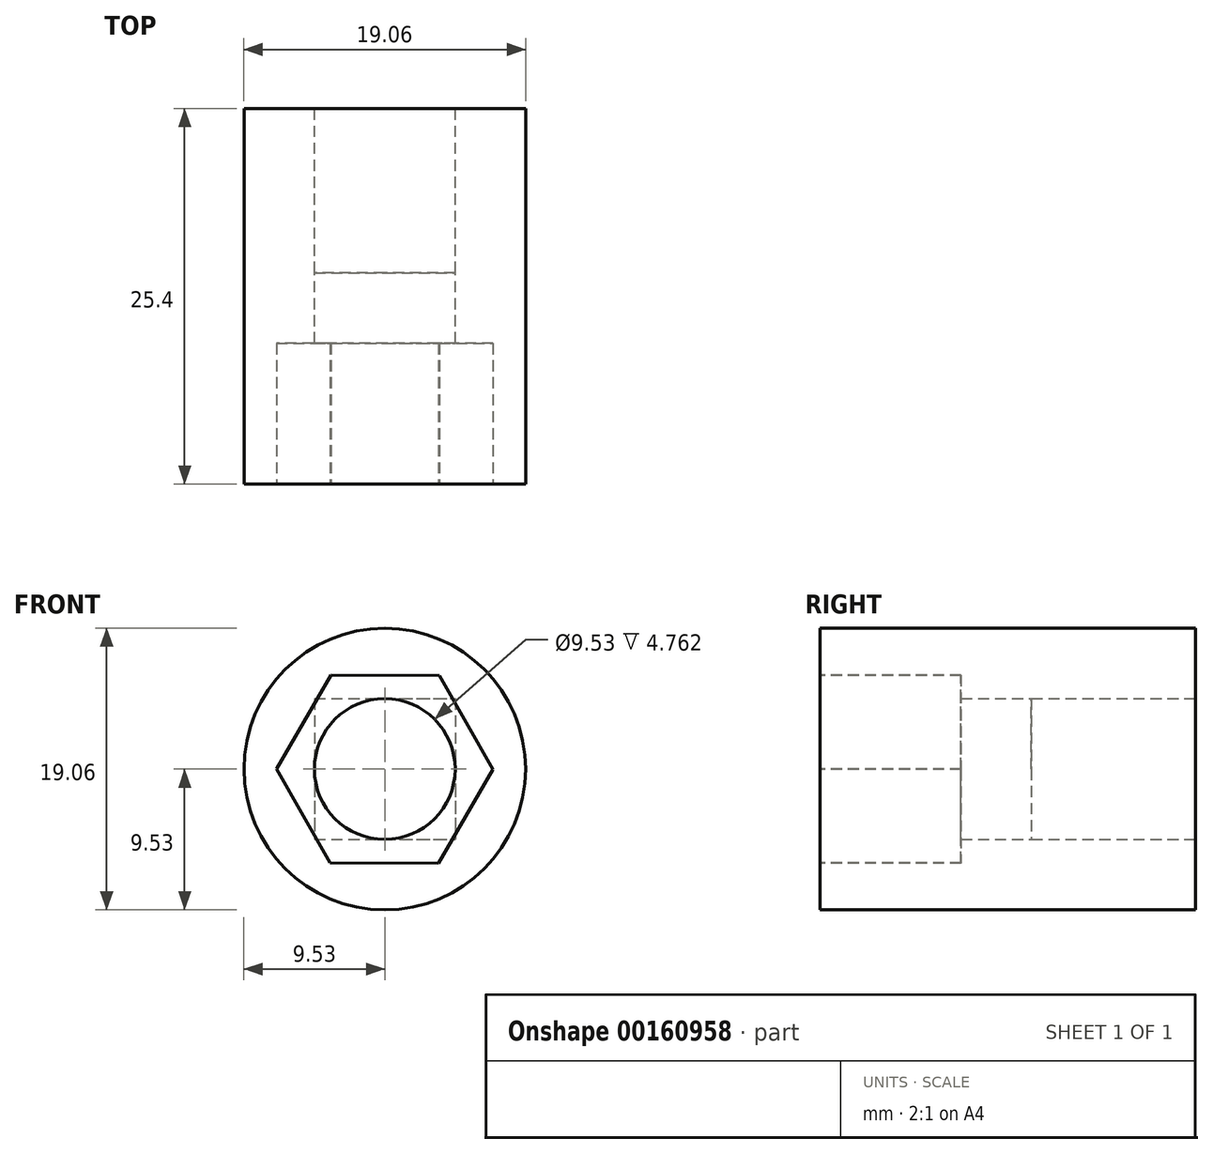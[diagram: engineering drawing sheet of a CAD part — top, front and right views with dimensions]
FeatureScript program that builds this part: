
annotation { "Feature Type Name" : "Feature", "Feature Type Description" : "" }
export const myFeature = defineFeature(function(context is Context, id is Id, definition is map)
    precondition{}
    {
        {
            var Q0;
            Q0=qCreatedBy(makeId("Front.planeOp"),FACE);
            var sketch = newSketch(context, id + "F0", { "sketchPlane" : qUnion([Q0])});
            skCircle(sketch, "E0", {"center": v(0, 0) * mm, "radius": 9.53 * mm});
            skSolve(sketch);
        }
        {
            var Q0;
            Q0 = qSketchRegion(id + "F0", true);
            extrude(context, id + "F1", {"entities" : qUnion([Q0]), "depth" : 25.4 * mm});
        }
        {
            var Q0;
            Q0=qCreatedBy(makeId("Front.planeOp"),FACE);
            var sketch = newSketch(context, id + "F2", { "sketchPlane" : qUnion([Q0])});
            skLineSegment(sketch, "E1.bottom", {"start": v(-4.76, 4.76) * mm, "end": v(4.76, 4.76) * mm});
            skLineSegment(sketch, "E1.top", {"start": v(-4.76, -4.76) * mm, "end": v(4.76, -4.76) * mm});
            skLineSegment(sketch, "E1.left", {"start": v(-4.76, 4.76) * mm, "end": v(-4.76, -4.76) * mm});
            skLineSegment(sketch, "E1.right", {"start": v(4.76, 4.76) * mm, "end": v(4.76, -4.76) * mm});
            skPoint(sketch, "E1.middle", {"position": v(0, 0) * mm});
            skCircle(sketch, "E2", {"center": v(0, 0) * mm, "radius": 4.76 * mm});
            skSolve(sketch);
        }
        {
            var Q0;
            {var subQ0=sQuery(id+"F2.wireOp",EDGE,"E2");var subQ1=makeQuery(id+"F2.imprint","INTERSECT",VERTEX,{"derivedFrom":[sQuery(id+"F2.wireOp",EDGE,"E1.bottom"),subQ0]});Q0=makeQuery(id+"F2.imprint","IMPRINT",FACE,{"disambiguationData":[TD([[makeQuery(id+"F2.imprint","IMPRINT",EDGE,{"disambiguationData":[TD([[subQ1,1.0]])],"derivedFrom":subQ0}),1.0]])]});}
            extrude(context, id + "F3", {"entities" : qUnion([Q0]), "operationType" : NewBodyOperationType.REMOVE, "endBound" : BoundingType.THROUGH_ALL, "depth" : 25.4 * mm});
        }
        {
            var Q0;
            Q0 = qSketchRegion(id + "F2", true);
            extrude(context, id + "F4", {"entities" : qUnion([Q0]), "operationType" : NewBodyOperationType.REMOVE, "depth" : 11.1 * mm});
        }
        {
            var Q0;
            Q0=makeQuery(id+"F1.opExtrude","CAP_FACE",FACE,{"disambiguationData":[OSD([sQuery(id+"F0.wireOp",EDGE,"E0")])],"isStart":false});
            var sketch = newSketch(context, id + "F5", { "sketchPlane" : qUnion([Q0])});
            skCircle(sketch, "E3.cCircle", {"center": v(0, 0) * mm, "radius": 7.33 * mm, "construction": true});
            skLineSegment(sketch, "E3.0", {"start": v(3.69, 6.34) * mm, "end": v(7.33, -0.02) * mm});
            skLineSegment(sketch, "E3.1", {"start": v(7.33, -0.02) * mm, "end": v(3.65, -6.36) * mm});
            skLineSegment(sketch, "E3.2", {"start": v(3.65, -6.36) * mm, "end": v(-3.69, -6.34) * mm});
            skLineSegment(sketch, "E3.3", {"start": v(-3.69, -6.34) * mm, "end": v(-7.33, 0.02) * mm});
            skLineSegment(sketch, "E3.4", {"start": v(-7.33, 0.02) * mm, "end": v(-3.65, 6.36) * mm});
            skLineSegment(sketch, "E3.5", {"start": v(-3.65, 6.36) * mm, "end": v(3.69, 6.34) * mm});
            skSolve(sketch);
        }
        {
            var Q0;
            Q0 = qSketchRegion(id + "F5", true);
            extrude(context, id + "F6", {"entities" : qUnion([Q0]), "operationType" : NewBodyOperationType.REMOVE, "oppositeDirection" : true, "depth" : 9.52 * mm});
        }
    });
